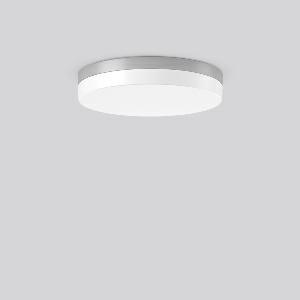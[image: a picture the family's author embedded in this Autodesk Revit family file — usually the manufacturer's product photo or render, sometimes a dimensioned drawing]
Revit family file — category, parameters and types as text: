
# Revit family: flat_slim_round_312632_004_76_c0e0
name_source: partatom
category: Lighting Fixtures
units: mm (PartAtom-declared; Revit-internal decimal feet)

## family parameters
Cut with Voids When Loaded = No
Host = Face
Light Source = No
Part Type = Normal
Room Calculation Point = No
Round Connector Dimension = Use Diameter
Shared = No

## types (1)
- MultiLumen 1 830 (1 x LED Modul 830, 2400 lm, 3000)
    Apparent Load = 20 VA
    CIE Flux Codes = 39 70 90 83 100
    Color Rendering = 80
    Color Temperature = 3000
    Default Elevation = 1800 mm
    Height = 70 mm
    Lamp = 1 x LED Modul 830
    Lamp Light Flux = 2400 lm
    Lamp count = 1
    Length = 400 mm
    Lifetime = 50000 h
    Luminous efficacy = 120 lm/W
    Manufacturer = RZB
    ModVariant = No
    Model = 312632.004.76
    Mounting Place = Ceiling
    Mounting Type = Surface mounted
    Number of Poles = 1
    OnlyDefault = Yes
    Power Factor = 1
    Product Name = FLAT SLIM round
    Product group = Surface mounted ceiling and wall luminaires
    ProductGroupID = 305
    Protection Class = Protection class I
    Protection Degree = Degree of protection
    RLX_Detail_Level = 1
    RLX_Emergency_Light_Flux = 0 lm
    RLX_Emergency_Type = 0
    RLX_Emergency_Type_DB = No
    RlxData = <blob elided: 20573 chars, md5=ba488e1f>
    Socket = socket
    Standby Power = 0 W
    System Light Flux = 2400 lm
    System Power = 20 W
    Type Comments = MultiLumen 1 830
    Type Image = 312631.004.jpg
    URL = http://relux.com
    VarID = multilumen_1_830
    Voltage = 0 V
    Weight = 0.00 kg
    Width = 0 mm  [stored 0 ft]

note: [stored X ft] marks values corroborated as IEEE doubles in the binary element streams (Revit-internal decimal feet)

## geometry (parser evidence)
native form markers: Blend x4, Sweep x12
no freeform markers — native parametric forms only
